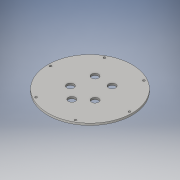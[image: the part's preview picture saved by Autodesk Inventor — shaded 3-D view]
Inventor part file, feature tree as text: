
AUTODESK INVENTOR PART (.ipt)
format: ipt  version: 2016 (Build 200138000, 138)  size: 131,072 bytes
history: native  units: in
note: dims shown in document units (in); Inventor stores cm internally (conversion verified against a paired STEP export)
features: extrude x2, sketch x2
ambient origin geometry x8: Origin, YZ Plane, XZ Plane, XY Plane, X Axis, Y Axis, Z Axis, Center Point
bodies: Solid1 (feature_tree)
feature tree (4):
  extrude  "Extrusion1"  Depth=0.1181in
  extrude  "Extrusion2"  Depth=0.108in TaperAngle=360.0deg
  sketch  "Sketch1"  dims[d0=4.63in d1=0.1181in]
  sketch  "Sketch2"  dims[d2=2.175in d3=2.3622in d5=360.0deg d7=0.108in d8=0.0in d9=0.393in d10=0.393in d11=0.47in d12=0.47in d13=0.747in d14=0.747in d15=1.0in d16=0.4in d17=0.4in d18=0.393in d19=0.393in d20=0.393in d21=0.68in d22=0.68in d23=0.108in d24=0.0in]
